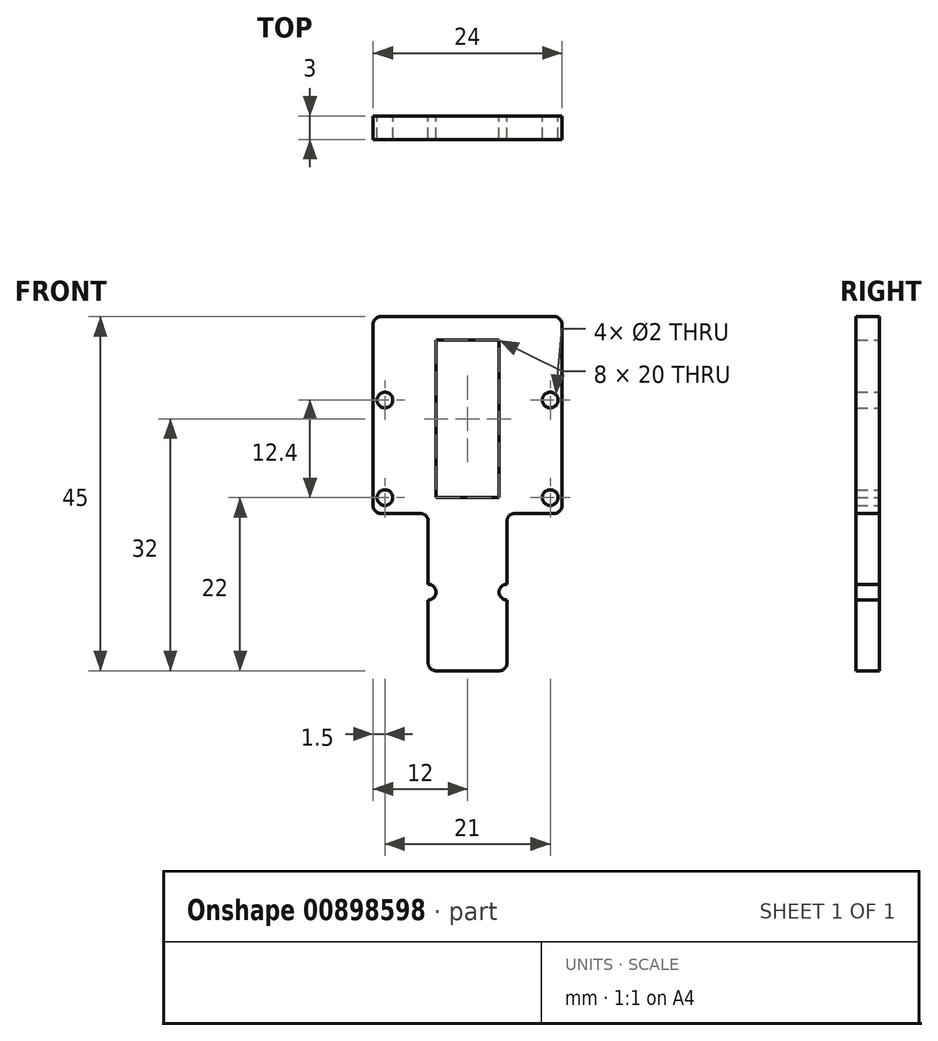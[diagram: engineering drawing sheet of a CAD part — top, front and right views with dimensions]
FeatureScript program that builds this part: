
annotation { "Feature Type Name" : "Feature", "Feature Type Description" : "" }
export const myFeature = defineFeature(function(context is Context, id is Id, definition is map)
    precondition{}
    {
        {
            var Q0;
            Q0=qCreatedBy(makeId("Front.planeOp"),FACE);
            var sketch = newSketch(context, id + "F0", { "sketchPlane" : qUnion([Q0])});
            skLineSegment(sketch, "E0.bottom", {"start": v(1, 0) * mm, "end": v(23, 0) * mm});
            skLineSegment(sketch, "E0.left", {"start": v(0, -1) * mm, "end": v(0, -24) * mm});
            skLineSegment(sketch, "E0.right", {"start": v(24, -1) * mm, "end": v(24, -24) * mm});
            skLineSegment(sketch, "E1", {"start": v(8, -45) * mm, "end": v(16, -45) * mm});
            skLineSegment(sketch, "E2", {"start": v(1, -25) * mm, "end": v(6, -25) * mm});
            skLineSegment(sketch, "E3", {"start": v(7, -26) * mm, "end": v(7, -34) * mm});
            skLineSegment(sketch, "E4", {"start": v(17, -44) * mm, "end": v(17, -36) * mm});
            skLineSegment(sketch, "E5", {"start": v(18, -25) * mm, "end": v(23, -25) * mm});
            skCircle(sketch, "E6", {"center": v(22.5, -23) * mm, "radius": 1 * mm});
            skCircle(sketch, "E7", {"center": v(1.5, -23) * mm, "radius": 1 * mm});
            skLineSegment(sketch, "E8", {"start": v(1.5, -23) * mm, "end": v(0, -23) * mm, "construction": true});
            skLineSegment(sketch, "E9", {"start": v(22.5, -23) * mm, "end": v(24, -23) * mm, "construction": true});
            skCircle(sketch, "E10", {"center": v(1.5, -10.6) * mm, "radius": 1 * mm});
            skCircle(sketch, "E11", {"center": v(22.5, -10.6) * mm, "radius": 1 * mm});
            skLineSegment(sketch, "E12", {"start": v(1.5, -10.6) * mm, "end": v(0, -10.6) * mm, "construction": true});
            skLineSegment(sketch, "E13", {"start": v(22.5, -10.6) * mm, "end": v(24, -10.6) * mm, "construction": true});
            skLineSegment(sketch, "E14.bottom", {"start": v(8, -3) * mm, "end": v(16, -3) * mm});
            skLineSegment(sketch, "E14.top", {"start": v(8, -23) * mm, "end": v(16, -23) * mm});
            skLineSegment(sketch, "E14.left", {"start": v(8, -3) * mm, "end": v(8, -23) * mm});
            skLineSegment(sketch, "E14.right", {"start": v(16, -3) * mm, "end": v(16, -23) * mm});
            skPoint(sketch, "E15", {"position": v(12, 0) * mm});
            skPoint(sketch, "E16", {"position": v(12, -3) * mm});
            skLineSegment(sketch, "E17", {"start": v(12, 0) * mm, "end": v(12, -3) * mm, "construction": true});
            skArc(sketch, "E18", {"start": v(7, -36) * mm, "mid": v(8, -35) * mm, "end": v(7, -34) * mm});
            skArc(sketch, "E19", {"start": v(17, -34) * mm, "mid": v(16, -35) * mm, "end": v(17, -36) * mm});
            skLineSegment(sketch, "E20.trimOffspring", {"start": v(7, -36) * mm, "end": v(7, -44) * mm});
            skLineSegment(sketch, "E21.trimOffspring", {"start": v(17, -34) * mm, "end": v(17, -26) * mm});
            skPoint(sketch, "E22.visualSharp", {"position": v(0, 0) * mm});
            skArc(sketch, "E22.filletArc", {"start": v(1, 0) * mm, "mid": v(0.3, -0.3) * mm, "end": v(0, -1) * mm});
            skPoint(sketch, "E23.visualSharp", {"position": v(24, 0) * mm});
            skArc(sketch, "E23.filletArc", {"start": v(24, -1) * mm, "mid": v(23.7, -0.3) * mm, "end": v(23, 0) * mm});
            skPoint(sketch, "E24.visualSharp", {"position": v(24, -25) * mm});
            skArc(sketch, "E24.filletArc", {"start": v(23, -25) * mm, "mid": v(23.7, -24.7) * mm, "end": v(24, -24) * mm});
            skPoint(sketch, "E25.visualSharp", {"position": v(0, -25) * mm});
            skArc(sketch, "E25.filletArc", {"start": v(0, -24) * mm, "mid": v(0.3, -24.7) * mm, "end": v(1, -25) * mm});
            skPoint(sketch, "E26.visualSharp", {"position": v(7, -25) * mm});
            skArc(sketch, "E26.filletArc", {"start": v(7, -26) * mm, "mid": v(6.7, -25.3) * mm, "end": v(6, -25) * mm});
            skPoint(sketch, "E27.visualSharp", {"position": v(17, -25) * mm});
            skArc(sketch, "E27.filletArc", {"start": v(18, -25) * mm, "mid": v(17.3, -25.3) * mm, "end": v(17, -26) * mm});
            skPoint(sketch, "E28.visualSharp", {"position": v(17, -45) * mm});
            skArc(sketch, "E28.filletArc", {"start": v(16, -45) * mm, "mid": v(16.7, -44.7) * mm, "end": v(17, -44) * mm});
            skPoint(sketch, "E29.visualSharp", {"position": v(7, -45) * mm});
            skArc(sketch, "E29.filletArc", {"start": v(7, -44) * mm, "mid": v(7.3, -44.7) * mm, "end": v(8, -45) * mm});
            skSolve(sketch);
        }
        {
            var Q0;
            Q0=qSketchRegion(id+"F0",true);
            extrude(context, id + "F1", {"entities" : qUnion([Q0]), "depth" : 3 * mm});
        }
    });
